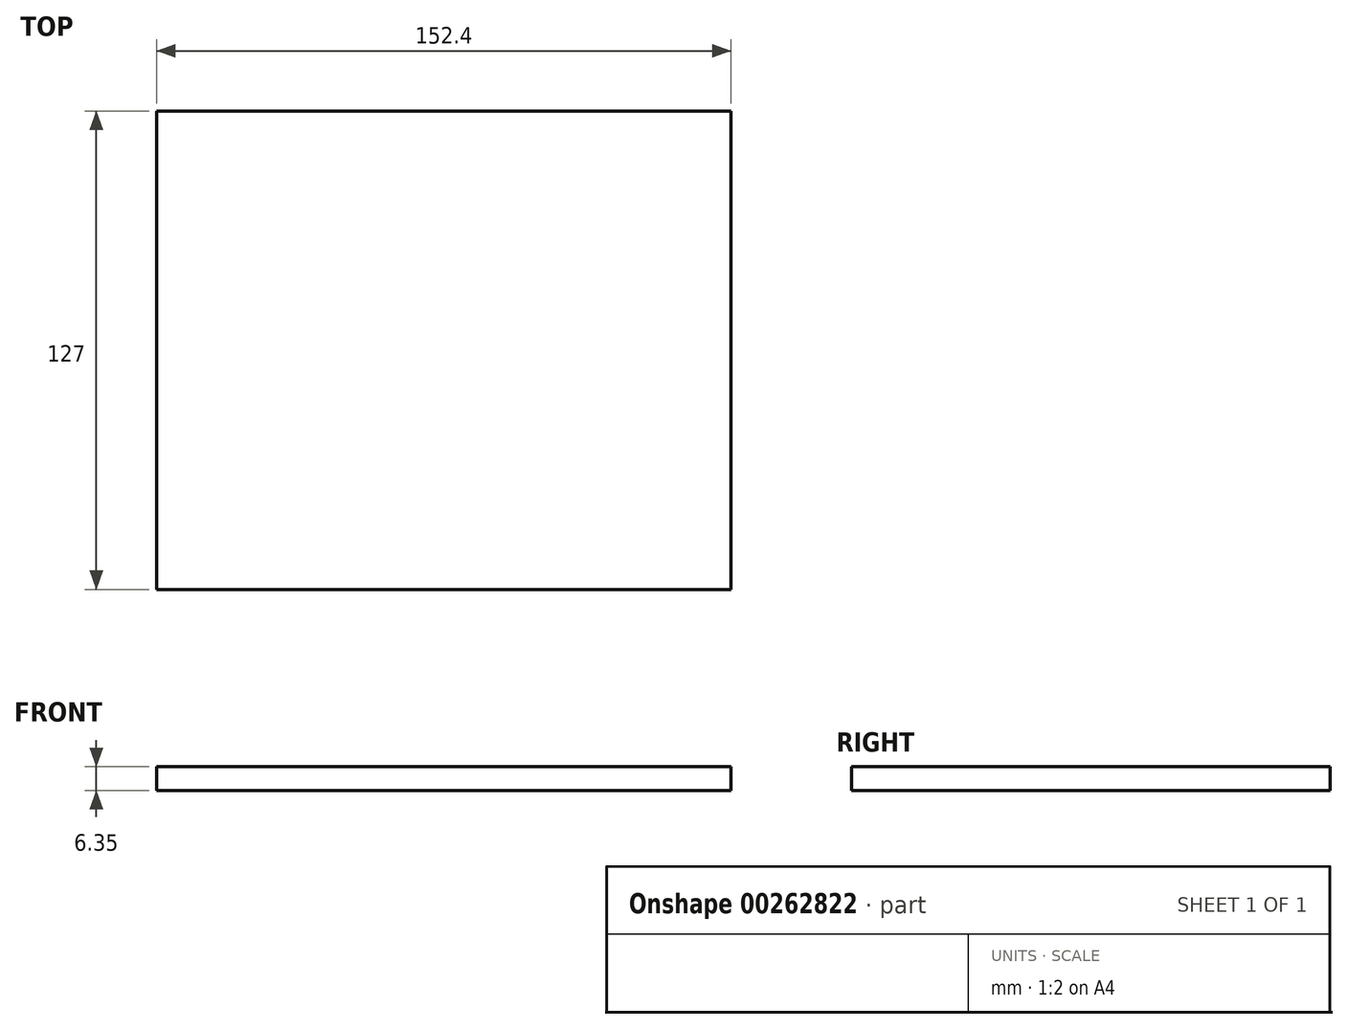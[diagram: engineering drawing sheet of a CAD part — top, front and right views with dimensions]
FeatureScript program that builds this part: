
annotation { "Feature Type Name" : "Feature", "Feature Type Description" : "" }
export const myFeature = defineFeature(function(context is Context, id is Id, definition is map)
    precondition{}
    {
        {
            var Q0;
            Q0=qCreatedBy(makeId("Top.planeOp"),FACE);
            var sketch = newSketch(context, id + "F0", { "sketchPlane" : qUnion([Q0])});
            skLineSegment(sketch, "E0.bottom", {"start": v(76.2, -63.5) * mm, "end": v(-76.2, -63.5) * mm});
            skLineSegment(sketch, "E0.top", {"start": v(76.2, 63.5) * mm, "end": v(-76.2, 63.5) * mm});
            skLineSegment(sketch, "E0.left", {"start": v(76.2, -63.5) * mm, "end": v(76.2, 63.5) * mm});
            skLineSegment(sketch, "E0.right", {"start": v(-76.2, -63.5) * mm, "end": v(-76.2, 63.5) * mm});
            skPoint(sketch, "E0.middle", {"position": v(0, 0) * mm});
            skSolve(sketch);
        }
        {
            var Q0;
            Q0 = qSketchRegion(id + "F0", true);
            extrude(context, id + "F1", {"entities" : qUnion([Q0]), "depth" : 6.35 * mm});
        }
    });
